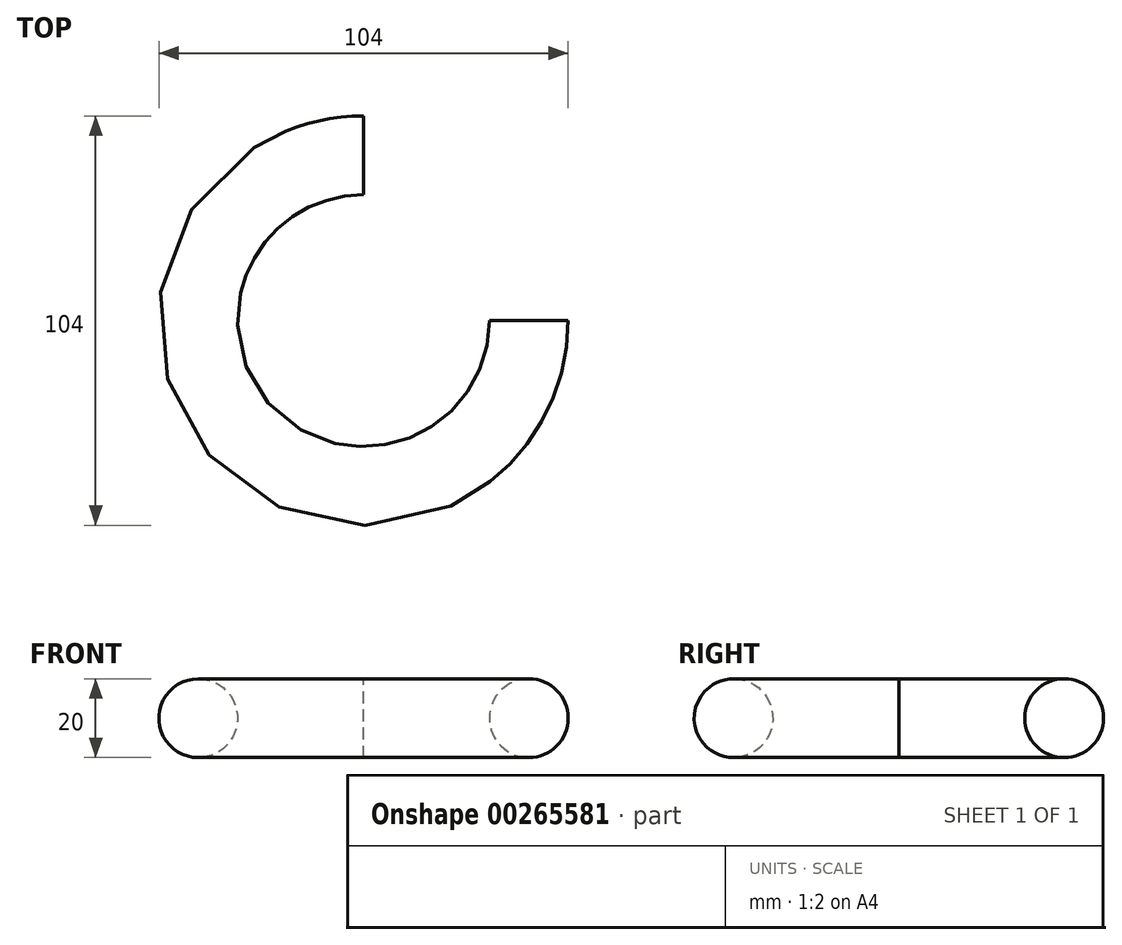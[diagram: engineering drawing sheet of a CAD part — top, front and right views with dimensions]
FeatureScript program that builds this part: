
annotation { "Feature Type Name" : "Feature", "Feature Type Description" : "" }
export const myFeature = defineFeature(function(context is Context, id is Id, definition is map)
    precondition{}
    {
        {
            var Q0;
            Q0=qCreatedBy(makeId("Front.planeOp"),FACE);
            var sketch = newSketch(context, id + "F0", { "sketchPlane" : qUnion([Q0])});
            skCircle(sketch, "E0", {"center": v(42, 0) * mm, "radius": 10 * mm});
            skLineSegment(sketch, "E1", {"start": v(0, 56.44) * mm, "end": v(0, -45.02) * mm, "construction": true});
            skSolve(sketch);
        }
        {
            var Q0;
            Q0=makeQuery(id+"F0.imprint","IMPRINT",FACE,{"disambiguationData":[TD([[makeQuery(id+"F0.imprint","IMPRINT",EDGE,{"derivedFrom":sQuery(id+"F0.wireOp",EDGE,"E0")}),1.0]])]});
            var Q1;
            Q1=sQuery(id+"F0.wireOp",EDGE,"E1");
            revolve(context, id + "F1", {"entities" : qUnion([Q0]), "axis" : qUnion([Q1]), "revolveType" : RevolveType.ONE_DIRECTION, "angle" : 270 * degree});
        }
    });
